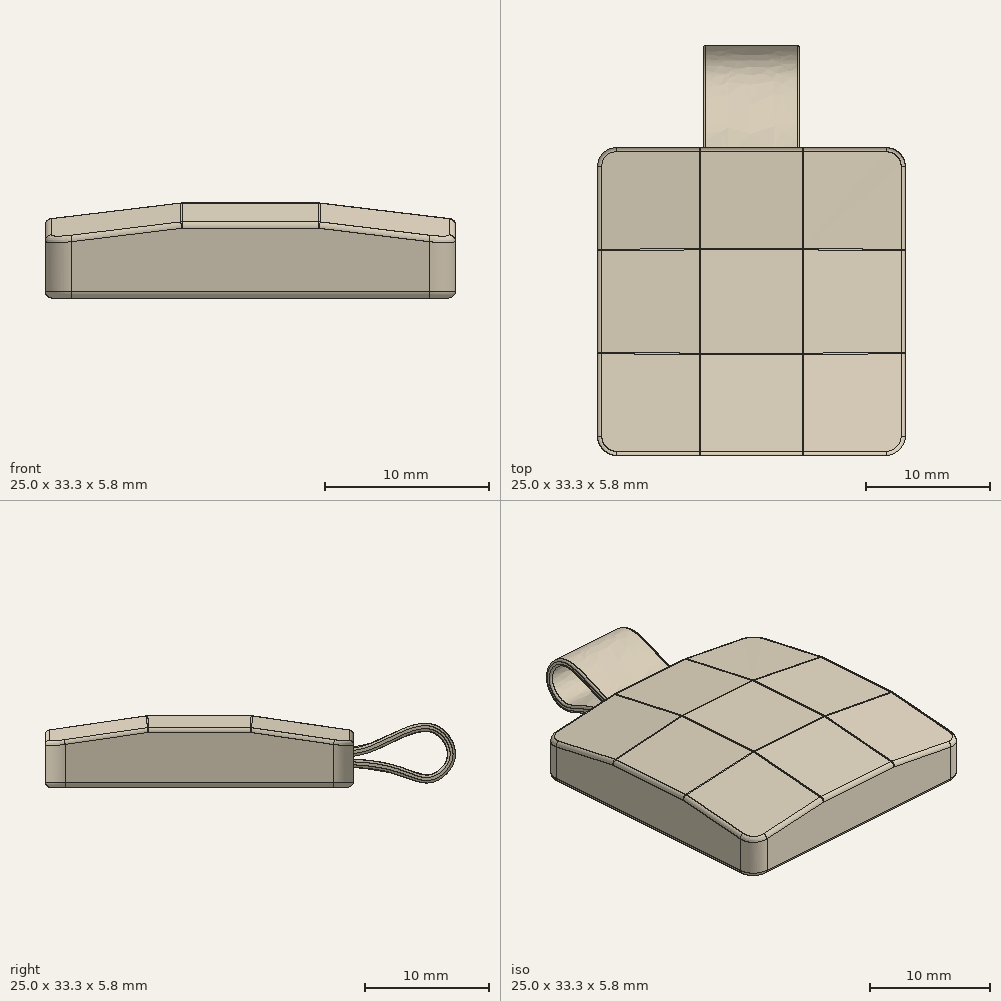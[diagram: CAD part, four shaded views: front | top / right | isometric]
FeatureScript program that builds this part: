
annotation { "Feature Type Name" : "Feature", "Feature Type Description" : "" }
export const myFeature = defineFeature(function(context is Context, id is Id, definition is map)
    precondition{}
    {
        {
            var Q0;
            Q0=qCreatedBy(makeId("Top.planeOp"),FACE);
            var sketch = newSketch(context, id + "F0", { "sketchPlane" : qUnion([Q0])});
            skLineSegment(sketch, "E0.bottom", {"start": v(-12.5, 12.5) * mm, "end": v(12.5, 12.5) * mm});
            skLineSegment(sketch, "E0.top", {"start": v(-12.5, -12.5) * mm, "end": v(12.5, -12.5) * mm});
            skLineSegment(sketch, "E0.left", {"start": v(-12.5, 12.5) * mm, "end": v(-12.5, -12.5) * mm});
            skLineSegment(sketch, "E0.right", {"start": v(12.5, 12.5) * mm, "end": v(12.5, -12.5) * mm});
            skPoint(sketch, "E0.middle", {"position": v(0, 0) * mm});
            skSolve(sketch);
        }
        {
            var Q0;
            Q0=qSketchRegion(id+"F0",true);
            extrude(context, id + "F1", {"entities" : qUnion([Q0]), "depth" : 4.6 * mm});
        }
        {
            var Q0;
            Q0=makeQuery(id+"F1.opExtrude","SWEPT_FACE",FACE,{"disambiguationData":[OSD([sQuery(id+"F0.wireOp",EDGE,"E0.right")])]});
            var sketch = newSketch(context, id + "F2", { "sketchPlane" : qUnion([Q0])});
            skLineSegment(sketch, "E1", {"start": v(-12.5, 4.6) * mm, "end": v(-4.25, 5.8) * mm});
            skLineSegment(sketch, "E2", {"start": v(-4.25, 5.8) * mm, "end": v(4.25, 5.8) * mm});
            skLineSegment(sketch, "E3", {"start": v(4.25, 5.8) * mm, "end": v(12.5, 4.6) * mm});
            skLineSegment(sketch, "E4", {"start": v(0, 0) * mm, "end": v(0, 5.8) * mm});
            skSolve(sketch);
        }
        {
            var Q0;
            {var subQ0=sQuery(id+"F2.wireOp",EDGE,"E3");Q0=makeQuery(id+"F2.imprint","IMPRINT",FACE,{"disambiguationData":[TD([[makeQuery(id+"F2.imprint","IMPRINT",EDGE,{"derivedFrom":subQ0}),-1.0]])]});}
            var Q1;
            {var subQ0=sQuery(id+"F2.wireOp",EDGE,"E1");Q1=makeQuery(id+"F2.imprint","IMPRINT",FACE,{"disambiguationData":[TD([[makeQuery(id+"F2.imprint","IMPRINT",EDGE,{"derivedFrom":subQ0}),-1.0]])]});}
            var Q2;
            Q2=makeQuery(id+"F1.opExtrude","SWEPT_FACE",FACE,{"disambiguationData":[OSD([sQuery(id+"F0.wireOp",EDGE,"E0.left")])]});
            extrude(context, id + "F3", {"entities" : qUnion([Q0, Q1]), "operationType" : NewBodyOperationType.ADD, "endBound" : BoundingType.UP_TO_SURFACE, "oppositeDirection" : true, "endBoundEntityFace" : qUnion([Q2]), "depth" : 25 * mm});
        }
        {
            var Q0;
            Q0=makeQuery(id+"F3.opExtrude","CAP_EDGE",EDGE,{"disambiguationData":[OSD([sQuery(id+"F2.wireOp",EDGE,"E2")])],"isStart":false});
            var Q1;
            Q1=makeQuery(id+"F3.opExtrude","CAP_EDGE",EDGE,{"disambiguationData":[OSD([sQuery(id+"F2.wireOp",EDGE,"E1")])],"isStart":false});
            var Q2;
            Q2=makeQuery(id+"F3.opExtrude","CAP_EDGE",EDGE,{"disambiguationData":[OSD([sQuery(id+"F2.wireOp",EDGE,"E3")])],"isStart":false});
            var Q3;
            Q3=makeQuery(id+"F3.opExtrude","CAP_EDGE",EDGE,{"disambiguationData":[OSD([sQuery(id+"F2.wireOp",EDGE,"E3")])],"isStart":true});
            var Q4;
            Q4=makeQuery(id+"F3.opExtrude","CAP_EDGE",EDGE,{"disambiguationData":[OSD([sQuery(id+"F2.wireOp",EDGE,"E2")])],"isStart":true});
            var Q5;
            Q5=makeQuery(id+"F3.opExtrude","CAP_EDGE",EDGE,{"disambiguationData":[OSD([sQuery(id+"F2.wireOp",EDGE,"E1")])],"isStart":true});
            chamfer(context, id + "F4", {"entities" : qUnion([Q0, Q1, Q2, Q3, Q4, Q5]), "chamferType" : ChamferType.TWO_OFFSETS, "width1" : 8.3 * mm, "oppositeDirection" : false, "width2" : 1 * mm, "tangentPropagation" : true});
        }
        {
            var Q0;
            Q0=makeQuery(id+"F1.opExtrude","SWEPT_EDGE",EDGE,{"disambiguationData":[OSD([sQuery(id+"F0.wireOp",EDGE,"E0.top"),sQuery(id+"F0.wireOp",EDGE,"E0.left")])]});
            var Q1;
            Q1=makeQuery(id+"F1.opExtrude","SWEPT_EDGE",EDGE,{"disambiguationData":[OSD([sQuery(id+"F0.wireOp",EDGE,"E0.top"),sQuery(id+"F0.wireOp",EDGE,"E0.right")])]});
            var Q2;
            Q2=makeQuery(id+"F1.opExtrude","SWEPT_EDGE",EDGE,{"disambiguationData":[OSD([sQuery(id+"F0.wireOp",EDGE,"E0.bottom"),sQuery(id+"F0.wireOp",EDGE,"E0.right")])]});
            var Q3;
            Q3=makeQuery(id+"F1.opExtrude","SWEPT_EDGE",EDGE,{"disambiguationData":[OSD([sQuery(id+"F0.wireOp",EDGE,"E0.bottom"),sQuery(id+"F0.wireOp",EDGE,"E0.left")])]});
            fillet(context, id + "F5", {"entities" : qUnion([Q0, Q1, Q2, Q3]), "radius" : 1.6 * mm, "tangentPropagation" : true, "allowEdgeOverflow" : false});
        }
        {
            var Q0;
            {var subQ0=sQuery(id+"F2.wireOp",EDGE,"E3");Q0=makeQuery(id+"F4.opChamfer","BLEND_EDGE",EDGE,{"blendedFrom":[makeQuery(id+"F3.opExtrude","CAP_EDGE",EDGE,{"disambiguationData":[OSD([subQ0])],"isStart":false}),makeQuery(id+"F3.opExtrude","SWEPT_FACE",FACE,{"disambiguationData":[OSD([subQ0])]})],"blendedInto":[makeQuery(id+"F3.opExtrude","SWEPT_FACE",FACE,{"disambiguationData":[OSD([subQ0])]})]});}
            var Q1;
            {var subQ0=sQuery(id+"F2.wireOp",EDGE,"E3");Q1=makeQuery(id+"F4.opChamfer","BLEND_EDGE",EDGE,{"blendedFrom":[makeQuery(id+"F3.opExtrude","CAP_EDGE",EDGE,{"disambiguationData":[OSD([subQ0])],"isStart":true}),makeQuery(id+"F3.opExtrude","SWEPT_FACE",FACE,{"disambiguationData":[OSD([subQ0])]})],"blendedInto":[makeQuery(id+"F3.opExtrude","SWEPT_FACE",FACE,{"disambiguationData":[OSD([subQ0])]})]});}
            var Q2;
            Q2=makeQuery(id+"F4.opChamfer","BLEND_EDGE",EDGE,{"blendedFrom":[makeQuery(id+"F3.opExtrude","CAP_EDGE",EDGE,{"disambiguationData":[OSD([sQuery(id+"F2.wireOp",EDGE,"E2")])],"isStart":true}),makeQuery(id+"F3.opExtrude","CAP_EDGE",EDGE,{"disambiguationData":[OSD([sQuery(id+"F2.wireOp",EDGE,"E3")])],"isStart":true})],"blendedInto":[]});
            var Q3;
            Q3=makeQuery(id+"F3.opExtrude","SWEPT_EDGE",EDGE,{"disambiguationData":[OSD([sQuery(id+"F2.wireOp",EDGE,"E2"),sQuery(id+"F2.wireOp",EDGE,"E3")])]});
            var Q4;
            Q4=makeQuery(id+"F4.opChamfer","BLEND_EDGE",EDGE,{"blendedFrom":[makeQuery(id+"F3.opExtrude","CAP_EDGE",EDGE,{"disambiguationData":[OSD([sQuery(id+"F2.wireOp",EDGE,"E2")])],"isStart":false}),makeQuery(id+"F3.opExtrude","CAP_EDGE",EDGE,{"disambiguationData":[OSD([sQuery(id+"F2.wireOp",EDGE,"E3")])],"isStart":false})],"blendedInto":[]});
            var Q5;
            {var subQ0=sQuery(id+"F2.wireOp",EDGE,"E2");Q5=makeQuery(id+"F4.opChamfer","BLEND_EDGE",EDGE,{"blendedFrom":[makeQuery(id+"F3.opExtrude","CAP_EDGE",EDGE,{"disambiguationData":[OSD([subQ0])],"isStart":false}),makeQuery(id+"F3.opExtrude","SWEPT_FACE",FACE,{"disambiguationData":[OSD([subQ0])]})],"blendedInto":[makeQuery(id+"F3.opExtrude","SWEPT_FACE",FACE,{"disambiguationData":[OSD([subQ0])]})]});}
            var Q6;
            {var subQ0=sQuery(id+"F2.wireOp",EDGE,"E2");Q6=makeQuery(id+"F4.opChamfer","BLEND_EDGE",EDGE,{"blendedFrom":[makeQuery(id+"F3.opExtrude","CAP_EDGE",EDGE,{"disambiguationData":[OSD([subQ0])],"isStart":true}),makeQuery(id+"F3.opExtrude","SWEPT_FACE",FACE,{"disambiguationData":[OSD([subQ0])]})],"blendedInto":[makeQuery(id+"F3.opExtrude","SWEPT_FACE",FACE,{"disambiguationData":[OSD([subQ0])]})]});}
            var Q7;
            Q7=makeQuery(id+"F4.opChamfer","BLEND_EDGE",EDGE,{"blendedFrom":[makeQuery(id+"F3.opExtrude","CAP_EDGE",EDGE,{"disambiguationData":[OSD([sQuery(id+"F2.wireOp",EDGE,"E1")])],"isStart":true}),makeQuery(id+"F3.opExtrude","CAP_EDGE",EDGE,{"disambiguationData":[OSD([sQuery(id+"F2.wireOp",EDGE,"E2")])],"isStart":true})],"blendedInto":[]});
            var Q8;
            {var subQ0=sQuery(id+"F2.wireOp",EDGE,"E1");Q8=makeQuery(id+"F4.opChamfer","BLEND_EDGE",EDGE,{"blendedFrom":[makeQuery(id+"F3.opExtrude","CAP_EDGE",EDGE,{"disambiguationData":[OSD([subQ0])],"isStart":true}),makeQuery(id+"F3.opExtrude","SWEPT_FACE",FACE,{"disambiguationData":[OSD([subQ0])]})],"blendedInto":[makeQuery(id+"F3.opExtrude","SWEPT_FACE",FACE,{"disambiguationData":[OSD([subQ0])]})]});}
            var Q9;
            Q9=makeQuery(id+"F3.opExtrude","SWEPT_EDGE",EDGE,{"disambiguationData":[OSD([sQuery(id+"F2.wireOp",EDGE,"E1"),sQuery(id+"F2.wireOp",EDGE,"E2")])]});
            var Q10;
            {var subQ0=sQuery(id+"F2.wireOp",EDGE,"E1");Q10=makeQuery(id+"F4.opChamfer","BLEND_EDGE",EDGE,{"blendedFrom":[makeQuery(id+"F3.opExtrude","CAP_EDGE",EDGE,{"disambiguationData":[OSD([subQ0])],"isStart":false}),makeQuery(id+"F3.opExtrude","SWEPT_FACE",FACE,{"disambiguationData":[OSD([subQ0])]})],"blendedInto":[makeQuery(id+"F3.opExtrude","SWEPT_FACE",FACE,{"disambiguationData":[OSD([subQ0])]})]});}
            var Q11;
            Q11=makeQuery(id+"F4.opChamfer","BLEND_EDGE",EDGE,{"blendedFrom":[makeQuery(id+"F3.opExtrude","CAP_EDGE",EDGE,{"disambiguationData":[OSD([sQuery(id+"F2.wireOp",EDGE,"E1")])],"isStart":false}),makeQuery(id+"F3.opExtrude","CAP_EDGE",EDGE,{"disambiguationData":[OSD([sQuery(id+"F2.wireOp",EDGE,"E2")])],"isStart":false})],"blendedInto":[]});
            fillet(context, id + "F6", {"entities" : qUnion([Q0, Q1, Q2, Q3, Q4, Q5, Q6, Q7, Q8, Q9, Q10, Q11]), "radius" : 0.8 * mm, "tangentPropagation" : true, "allowEdgeOverflow" : false});
        }
        {
            var Q0;
            {var subQ0=sQuery(id+"F2.wireOp",EDGE,"E3");Q0=makeQuery(id+"F4.opChamfer","BLEND_EDGE",EDGE,{"blendedFrom":[makeQuery(id+"F3.opExtrude","CAP_EDGE",EDGE,{"disambiguationData":[OSD([subQ0])],"isStart":false}),makeQuery(id+"F3.boolean.opBoolean","MERGE",FACE,{"derivedFrom":[makeQuery(id+"F1.opExtrude","SWEPT_FACE",FACE,{"disambiguationData":[OSD([sQuery(id+"F0.wireOp",EDGE,"E0.left")])]}),makeQuery(id+"F3.opExtrude","CAP_FACE",FACE,{"disambiguationData":[OSD([sQuery(id+"F0.wireOp",EDGE,"E0.right"),sQuery(id+"F2.wireOp",EDGE,"E1"),sQuery(id+"F2.wireOp",EDGE,"E2"),subQ0])],"isStart":false})]})],"blendedInto":[makeQuery(id+"F3.boolean.opBoolean","MERGE",FACE,{"derivedFrom":[makeQuery(id+"F1.opExtrude","SWEPT_FACE",FACE,{"disambiguationData":[OSD([sQuery(id+"F0.wireOp",EDGE,"E0.left")])]}),makeQuery(id+"F3.opExtrude","CAP_FACE",FACE,{"disambiguationData":[OSD([sQuery(id+"F0.wireOp",EDGE,"E0.right"),sQuery(id+"F2.wireOp",EDGE,"E1"),sQuery(id+"F2.wireOp",EDGE,"E2"),subQ0])],"isStart":false})]})]});}
            var Q1;
            Q1=makeQuery(id+"F1.opExtrude","CAP_EDGE",EDGE,{"disambiguationData":[OSD([sQuery(id+"F0.wireOp",EDGE,"E0.left")])],"isStart":true});
            fillet(context, id + "F7", {"entities" : qUnion([Q0, Q1]), "radius" : 0.4 * mm, "tangentPropagation" : true, "allowEdgeOverflow" : false});
        }
        {
            var Q0;
            Q0=makeQuery(id+"F1.opExtrude","CAP_FACE",FACE,{"disambiguationData":[OSD([sQuery(id+"F0.wireOp",EDGE,"E0.bottom"),sQuery(id+"F0.wireOp",EDGE,"E0.top"),sQuery(id+"F0.wireOp",EDGE,"E0.left"),sQuery(id+"F0.wireOp",EDGE,"E0.right")])],"isStart":true});
            var sketch = newSketch(context, id + "F8", { "sketchPlane" : qUnion([Q0])});
            skLineSegment(sketch, "E5.bottom", {"start": v(-4, -8.1) * mm, "end": v(4, -8.1) * mm});
            skLineSegment(sketch, "E5.top", {"start": v(-4, -16.1) * mm, "end": v(4, -16.1) * mm});
            skLineSegment(sketch, "E5.left", {"start": v(-4, -8.1) * mm, "end": v(-4, -16.1) * mm});
            skLineSegment(sketch, "E5.right", {"start": v(4, -8.1) * mm, "end": v(4, -16.1) * mm});
            skPoint(sketch, "E5.middle", {"position": v(0, -12.1) * mm});
            skSolve(sketch);
        }
        {
            var Q0;
            Q0 = qSketchRegion(id + "F8", true);
            extrude(context, id + "F9", {"entities" : qUnion([Q0]), "operationType" : NewBodyOperationType.REMOVE, "oppositeDirection" : true, "depth" : (1.6 + 1.6) * mm, "hasSecondDirection" : true, "secondDirectionOppositeDirection" : true, "secondDirectionDepth" : 1.6 * mm});
        }
        {
            var Q0;
            Q0=qCreatedBy(makeId("Right.planeOp"),FACE);
            var sketch = newSketch(context, id + "F10", { "sketchPlane" : qUnion([Q0])});
            skLineSegment(sketch, "E6.0", {"start": v(8.1, 3.2) * mm, "end": v(8.1, 1.6) * mm});
            skFitSpline(sketch, "E7", {"points": [v(8.1, 3.11) * mm, v(13.74, 3.48) * mm, v(18.77, 5.16) * mm, v(20.78, 2.53) * mm, v(18.9, 0.38) * mm, v(15.25, 1.26) * mm, v(8.1, 1.68) * mm], "startDerivative": vector(42.5, 0.85) * mm, "endDerivative": vector(-23.92, 0) * mm});
            skFitSpline(sketch, "E8.0", {"points": [v(8.11, 2.46) * mm, v(8.98, 2.48) * mm, v(10.07, 2.45) * mm, v(11.32, 2.44) * mm, v(12.21, 2.47) * mm, v(12.95, 2.58) * mm, v(13.55, 2.73) * mm, v(14.01, 2.88) * mm, v(14.47, 3.07) * mm, v(15.08, 3.34) * mm, v(15.84, 3.71) * mm, v(16.73, 4.13) * mm, v(17.42, 4.39) * mm, v(17.91, 4.5) * mm, v(18.25, 4.55) * mm, v(18.54, 4.54) * mm, v(18.89, 4.47) * mm, v(19.32, 4.24) * mm, v(19.76, 3.8) * mm, v(20.06, 3.24) * mm, v(20.15, 2.77) * mm, v(20.13, 2.45) * mm, v(20.04, 2.12) * mm, v(19.82, 1.72) * mm, v(19.49, 1.38) * mm, v(19.2, 1.18) * mm, v(18.96, 1.07) * mm, v(18.75, 1) * mm, v(18.54, 0.98) * mm, v(18.31, 1) * mm, v(17.97, 1.05) * mm, v(17.44, 1.22) * mm, v(16.67, 1.5) * mm, v(15.9, 1.77) * mm, v(15.2, 1.94) * mm, v(14.47, 2.08) * mm, v(13.5, 2.2) * mm, v(12.28, 2.3) * mm, v(11.08, 2.34) * mm, v(9.56, 2.35) * mm, v(8.6, 2.33) * mm, v(8.1, 2.33) * mm]});
            skLineSegment(sketch, "E9", {"start": v(8.57, 3.12) * mm, "end": v(8.57, 1.69) * mm});
            skSolve(sketch);
        }
        {
            var Q0;
            {var subQ0=sQuery(id+"F10.wireOp",EDGE,"E9");var subQ1=sQuery(id+"F10.wireOp",EDGE,"E7");var subQ2=makeQuery(id+"F10.imprint","INTERSECT",VERTEX,{"disambiguationData":[OD(0.0)],"derivedFrom":[subQ1,subQ0]});Q0=makeQuery(id+"F10.imprint","IMPRINT",FACE,{"disambiguationData":[TD([[makeQuery(id+"F10.imprint","IMPRINT",EDGE,{"disambiguationData":[TD([[subQ2,-1.0]])],"derivedFrom":subQ1}),-1.0]])]});}
            extrude(context, id + "F11", {"entities" : qUnion([Q0]), "depth" : 3.9 * mm, "hasSecondDirection" : true, "secondDirectionOppositeDirection" : true, "secondDirectionDepth" : 3.9 * mm});
        }
        {
            var Q0;
            Q0=makeQuery(id+"F11.opExtrude","CAP_EDGE",EDGE,{"disambiguationData":[OSD([sQuery(id+"F10.wireOp",EDGE,"E8.0")])],"isStart":true});
            var Q1;
            Q1=makeQuery(id+"F11.opExtrude","CAP_EDGE",EDGE,{"disambiguationData":[OSD([sQuery(id+"F10.wireOp",EDGE,"E7")])],"isStart":true});
            var Q2;
            Q2=makeQuery(id+"F11.opExtrude","CAP_EDGE",EDGE,{"disambiguationData":[OSD([sQuery(id+"F10.wireOp",EDGE,"E7")])],"isStart":false});
            var Q3;
            Q3=makeQuery(id+"F11.opExtrude","CAP_EDGE",EDGE,{"disambiguationData":[OSD([sQuery(id+"F10.wireOp",EDGE,"E8.0")])],"isStart":false});
            fillet(context, id + "F12", {"entities" : qUnion([Q0, Q1, Q2, Q3]), "radius" : 0.2 * mm, "tangentPropagation" : true, "allowEdgeOverflow" : false});
        }
        {
            var Q0;
            Q0=makeQuery(id+"F9.boolean.opBoolean","COPY",EDGE,{"derivedFrom":makeQuery(id+"F9.opExtrude","CAP_EDGE",EDGE,{"disambiguationData":[OSD([sQuery(id+"F8.wireOp",EDGE,"E5.left")])],"isStart":true})});
            var Q1;
            Q1=makeQuery(id+"F9.boolean.opBoolean","COPY",EDGE,{"derivedFrom":makeQuery(id+"F9.opExtrude","CAP_EDGE",EDGE,{"disambiguationData":[OSD([sQuery(id+"F8.wireOp",EDGE,"E5.left")])],"isStart":false})});
            var Q2;
            Q2=makeQuery(id+"F9.boolean.opBoolean","COPY",EDGE,{"derivedFrom":makeQuery(id+"F9.opExtrude","CAP_EDGE",EDGE,{"disambiguationData":[OSD([sQuery(id+"F8.wireOp",EDGE,"E5.right")])],"isStart":true})});
            var Q3;
            Q3=makeQuery(id+"F9.boolean.opBoolean","COPY",EDGE,{"derivedFrom":makeQuery(id+"F9.opExtrude","CAP_EDGE",EDGE,{"disambiguationData":[OSD([sQuery(id+"F8.wireOp",EDGE,"E5.right")])],"isStart":false})});
            fillet(context, id + "F13", {"entities" : qUnion([Q0, Q1, Q2, Q3]), "radius" : 0.3 * mm, "tangentPropagation" : true, "allowEdgeOverflow" : false});
        }
        {
            var Q0;
            Q0=makeQuery(id+"F9.boolean.opBoolean","INTERSECT",EDGE,{"derivedFrom":[makeQuery(id+"F1.opExtrude","SWEPT_FACE",FACE,{"disambiguationData":[OSD([sQuery(id+"F0.wireOp",EDGE,"E0.bottom")])]}),makeQuery(id+"F9.opExtrude","CAP_FACE",FACE,{"disambiguationData":[OSD([sQuery(id+"F8.wireOp",EDGE,"E5.bottom"),sQuery(id+"F8.wireOp",EDGE,"E5.top"),sQuery(id+"F8.wireOp",EDGE,"E5.left"),sQuery(id+"F8.wireOp",EDGE,"E5.right")])],"isStart":true})]});
            fillet(context, id + "F14", {"entities" : qUnion([Q0]), "radius" : 0.1 * mm, "tangentPropagation" : true, "allowEdgeOverflow" : false});
        }
    });
